# Revit family: HDZCSA1-WALL
name_source: partatom
category: Lighting Fixtures
units: mm (PartAtom-declared; Revit-internal decimal feet)

## family parameters
Always vertical = Yes
Cut with Voids When Loaded = No
Host = Wall
Light Source = Yes
Maintain Annotation Orientation = No
Part Type = Normal
Room Calculation Point = No
Round Connector Dimension = Use Diameter
Shared = No

## types (1)
- HDZCSA1
    ACCESORY MATERIAL = LENS MATERIAL
    Color Filter = 16777215
    Default Elevation = 0' - 0"
    Description = HAZARDOUS EMERGENCY LIGHT
    Dimming Lamp Color Temperature Shift = <None>
    Emit from Line Length = 2' - 0"
    FACE MATERIAL = FACE MATERIAL TRANSPARENT
    HOUSING MATERIAL = HOUSING MATERIAL
    LED BOARD MATERIAL = LED BOARD MATERIAL
    LED MATERIAL = LED MATERIAL
    LENS MATERIAL = LENS MATERIAL
    LETTER MATERIAL = LETTER MATERIAL RED
    Lamp = LED
    MOUNTING HEIGHT = 8' - 0"
    Manufacturer = BEGHELLI
    Model = HDZCSA1
    Photometric Web File = HDZCSA1.ies
    Tilt Angle = 180.00°
    Type Image = HDZCSA1 IMAGE.png
    Wattage Comments = 16W

## geometry (parser evidence)
native form markers: Sweep x12
no freeform markers — native parametric forms only
